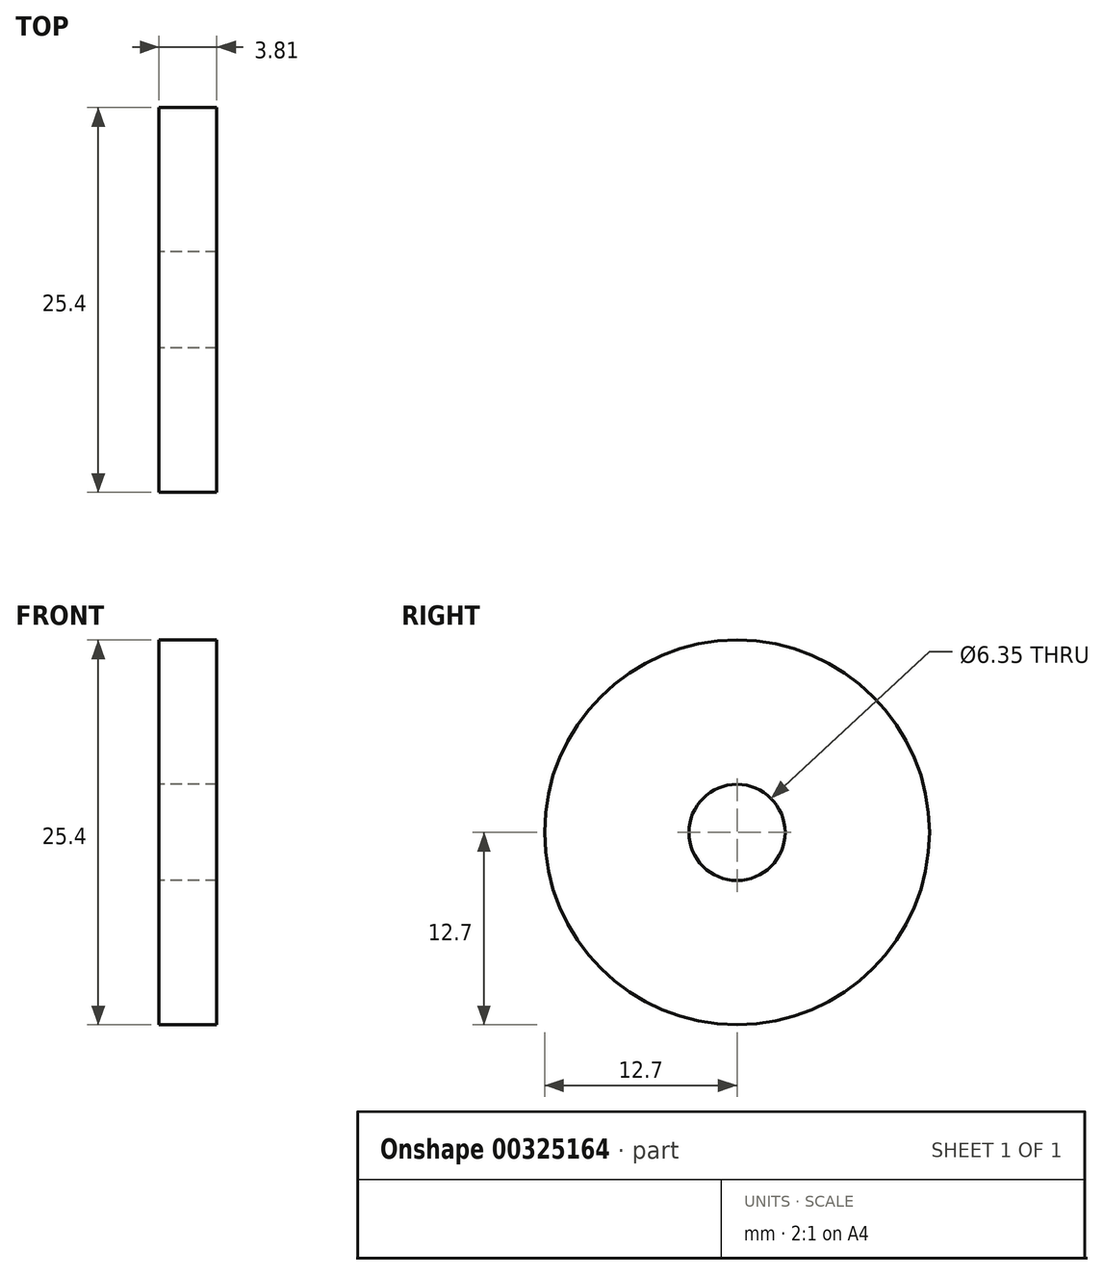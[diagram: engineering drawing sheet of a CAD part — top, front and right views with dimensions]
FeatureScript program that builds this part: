
annotation { "Feature Type Name" : "Feature", "Feature Type Description" : "" }
export const myFeature = defineFeature(function(context is Context, id is Id, definition is map)
    precondition{}
    {
        {
            var Q0;
            Q0=qCreatedBy(makeId("Right.planeOp"),FACE);
            var sketch = newSketch(context, id + "F0", { "sketchPlane" : qUnion([Q0])});
            skCircle(sketch, "E0", {"center": v(0, 0) * mm, "radius": 12.7 * mm});
            skCircle(sketch, "E1", {"center": v(0, 0) * mm, "radius": 3.18 * mm});
            skSolve(sketch);
        }
        {
            var Q0;
            Q0 = qSketchRegion(id + "F0", true);
            extrude(context, id + "F1", {"entities" : qUnion([Q0]), "depth" : 3.8 * mm});
        }
    });
